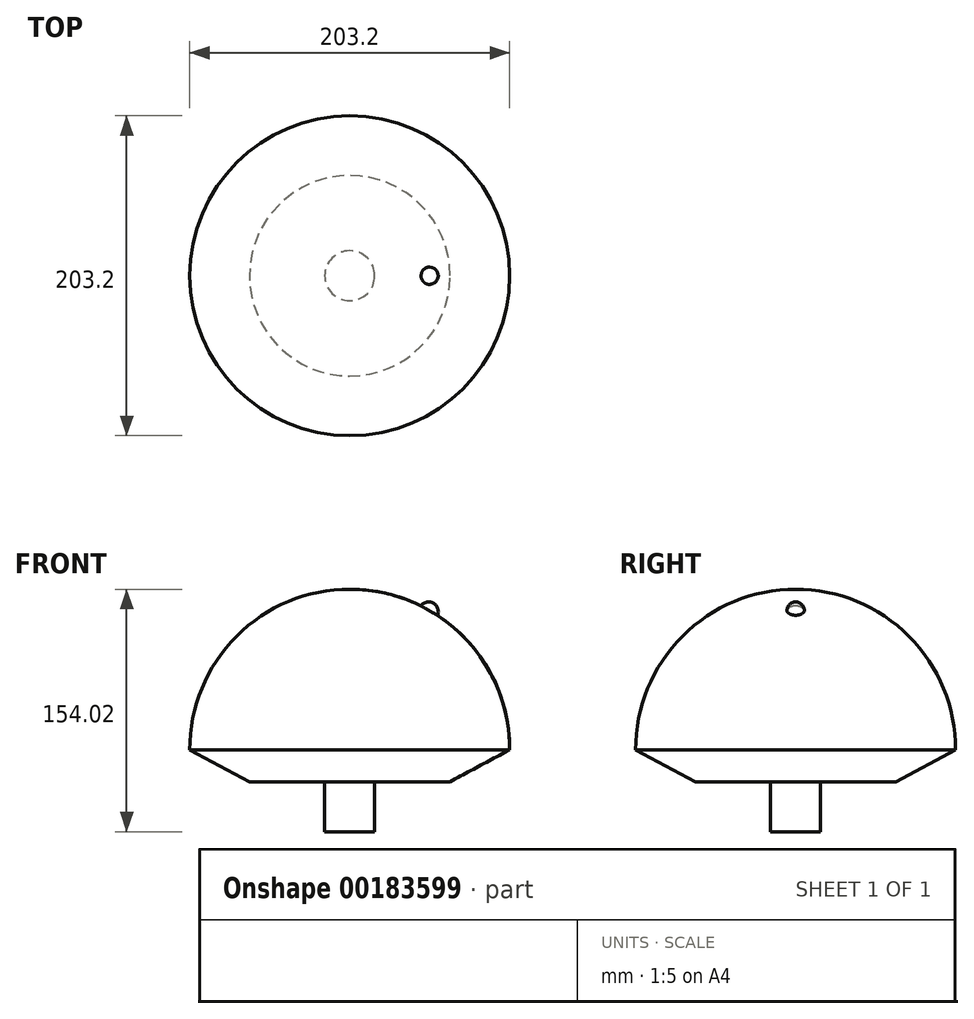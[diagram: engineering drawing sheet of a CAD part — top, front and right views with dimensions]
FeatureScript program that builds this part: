
annotation { "Feature Type Name" : "Feature", "Feature Type Description" : "" }
export const myFeature = defineFeature(function(context is Context, id is Id, definition is map)
    precondition{}
    {
        {
            var Q0;
            Q0=qCreatedBy(makeId("Front.planeOp"),FACE);
            var sketch = newSketch(context, id + "F0", { "sketchPlane" : qUnion([Q0])});
            skLineSegment(sketch, "E0", {"start": v(0, 101.95) * mm, "end": v(0, -20.32) * mm});
            skArc(sketch, "E1", {"start": v(101.6, 0) * mm, "mid": v(71.97, 72.07) * mm, "end": v(0, 101.95) * mm});
            skLineSegment(sketch, "E2", {"start": v(63.7, -20.32) * mm, "end": v(0, -20.32) * mm});
            skLineSegment(sketch, "E3", {"start": v(101.6, 0) * mm, "end": v(63.7, -20.32) * mm});
            skSolve(sketch);
        }
        {
            var Q0;
            Q0=makeQuery(id+"F0.imprint","IMPRINT",FACE,{"disambiguationData":[TD([[makeQuery(id+"F0.imprint","IMPRINT",EDGE,{"derivedFrom":sQuery(id+"F0.wireOp",EDGE,"E0")}),1.0]])]});
            var sketch = newSketch(context, id + "F1", { "sketchPlane" : qUnion([Q0])});
            skArc(sketch, "E4", {"start": v(55.63, 85.26) * mm, "mid": v(53.21, 93.08) * mm, "end": v(45.22, 91.35) * mm});
            skLineSegment(sketch, "E5", {"start": v(55.63, 85.26) * mm, "end": v(45.22, 91.35) * mm});
            skSolve(sketch);
        }
        {
            var Q0;
            {var subQ0=sQuery(id+"F1.wireOp",EDGE,"E5");var subQ1=sQuery(id+"F1.wireOp",EDGE,"E4");var subQ2=makeQuery(id+"F1.imprint","INTERSECT",VERTEX,{"disambiguationData":[OD(1.0)],"derivedFrom":[subQ1,subQ0]});Q0=makeQuery(id+"F1.imprint","IMPRINT",FACE,{"disambiguationData":[TD([[makeQuery(id+"F1.imprint","IMPRINT",EDGE,{"disambiguationData":[TD([[subQ2,1.0]])],"derivedFrom":subQ1}),1.0]])]});}
            var Q1;
            Q1=sQuery(id+"F1.wireOp",EDGE,"E5");
            revolve(context, id + "F2", {"entities" : qUnion([Q0]), "axis" : qUnion([Q1]), "revolveType" : RevolveType.FULL});
        }
        {
            var Q0;
            Q0=makeQuery(id+"F0.imprint","IMPRINT",FACE,{"disambiguationData":[TD([[makeQuery(id+"F0.imprint","IMPRINT",EDGE,{"derivedFrom":sQuery(id+"F0.wireOp",EDGE,"E0")}),1.0]])]});
            var Q1;
            Q1=sQuery(id+"F0.wireOp",EDGE,"E0");
            revolve(context, id + "F3", {"operationType" : NewBodyOperationType.ADD, "entities" : qUnion([Q0]), "axis" : qUnion([Q1]), "revolveType" : RevolveType.FULL});
        }
        {
            var Q0;
            Q0=makeQuery(id+"F3.opRevolve","SWEPT_FACE",FACE,{"disambiguationData":[OSD([sQuery(id+"F0.wireOp",EDGE,"E2")])]});
            var sketch = newSketch(context, id + "F4", { "sketchPlane" : qUnion([Q0])});
            skCircle(sketch, "E6", {"center": v(0, 0) * mm, "radius": 15.88 * mm});
            skSolve(sketch);
        }
        {
            var Q0;
            Q0=makeQuery(id+"F4.imprint","IMPRINT",FACE,{"disambiguationData":[TD([[makeQuery(id+"F4.imprint","IMPRINT",EDGE,{"derivedFrom":sQuery(id+"F4.wireOp",EDGE,"E6")}),1.0]])]});
            extrude(context, id + "F5", {"entities" : qUnion([Q0]), "operationType" : NewBodyOperationType.ADD, "depth" : 31.75 * mm});
        }
    });
